# Revit family: Showerhead-American_Standard-Square_Rain-1660_Series
name_source: partatom
category: Plumbing Fixtures
revit_build: Autodesk Revit 2015 (Build: 20140606_1530(x64)
units: mm (PartAtom-declared; Revit-internal decimal feet)

## types (2) — shared parameters
Assembly Code = D2010700
CW Connection = Yes
CWFU = 3
Description = 8 Inch Square Rain Showerhead
HW Connection = Yes
HWFU = 3
Height = 2"
Manufacturer = American Standard
Product Documentation Link = https://www.americanstandard-us.com
Product Page URL = https://www.americanstandard-us.com
Revised Date = 01/28/2020
Tempered Water Connection Diameter = 1/2"
Tempered Water Connection Radius = 1/4"
URL = http://www.americanstandard-us.com
Vent Connection = No
WFU = 4
Waste Connection = No
Width = 7 13/16"

## per-type parameters (varying)
| type | Finish | Material |
| 1660.688.002 | Brass-American Standard-002-Polished Chrome | Brass-American Standard-002-Polished Chrome |
| 1660.688.295 | Brass-American Standard-295-Brushed Nickel | Brass-American Standard-295-Brushed Nickel |

note: column(s) folded — value = type name in every type: Model

## geometry (parser evidence)
native form markers: Sweep x2
no freeform markers — native parametric forms only
